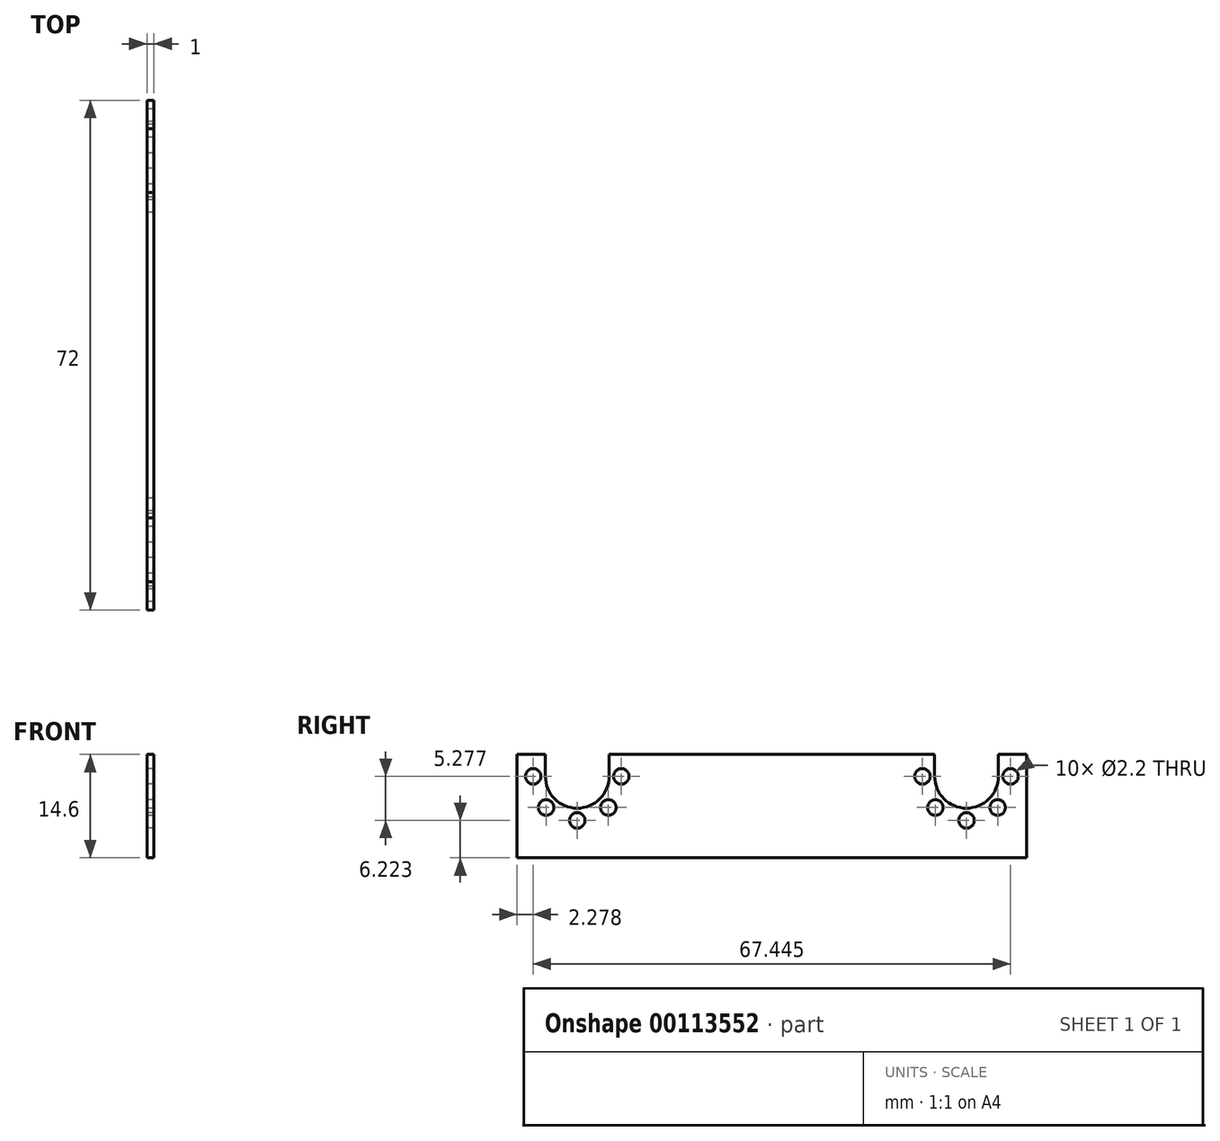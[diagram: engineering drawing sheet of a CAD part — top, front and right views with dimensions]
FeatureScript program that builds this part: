
annotation { "Feature Type Name" : "Feature", "Feature Type Description" : "" }
export const myFeature = defineFeature(function(context is Context, id is Id, definition is map)
    precondition{}
    {
        {
            var Q0;
            Q0=qCreatedBy(makeId("Front.planeOp"),FACE);
            var sketch = newSketch(context, id + "F0", { "sketchPlane" : qUnion([Q0])});
            skLineSegment(sketch, "E0", {"start": v(0, 20) * mm, "end": v(0, 0) * mm});
            skLineSegment(sketch, "E1", {"start": v(-1, 0) * mm, "end": v(-1, 20) * mm});
            skLineSegment(sketch, "E2", {"start": v(-1, 20) * mm, "end": v(0, 20) * mm});
            skLineSegment(sketch, "E3", {"start": v(-1, 0) * mm, "end": v(0, 0) * mm});
            skSolve(sketch);
        }
        {
            var Q0;
            Q0=qSketchRegion(id+"F0",true);
            extrude(context, id + "F1", {"entities" : qUnion([Q0]), "depth" : 72 * mm});
        }
        {
            var Q0;
            Q0=makeQuery(id+"F1.opExtrude","SWEPT_FACE",FACE,{"disambiguationData":[OSD([sQuery(id+"F0.wireOp",EDGE,"E1")])]});
            var sketch = newSketch(context, id + "F2", { "sketchPlane" : qUnion([Q0])});
            skArc(sketch, "E4", {"start": v(4, 11.5) * mm, "mid": v(8.5, 7) * mm, "end": v(13, 11.5) * mm});
            skCircle(sketch, "E5", {"center": v(2.28, 11.5) * mm, "radius": 1.1 * mm});
            skCircle(sketch, "E6.1.0", {"center": v(4.1, 7.1) * mm, "radius": 1.1 * mm});
            skCircle(sketch, "E6.2.0", {"center": v(8.5, 5.28) * mm, "radius": 1.1 * mm});
            skCircle(sketch, "E6.3.0", {"center": v(12.9, 7.1) * mm, "radius": 1.1 * mm});
            skCircle(sketch, "E7.1.4.0", {"center": v(14.72, 11.5) * mm, "radius": 1.1 * mm});
            skPoint(sketch, "E8", {"position": v(4, 11.5) * mm});
            skPoint(sketch, "E9", {"position": v(13, 11.5) * mm});
            skLineSegment(sketch, "E10", {"start": v(4, 11.5) * mm, "end": v(4, 20) * mm});
            skLineSegment(sketch, "E11", {"start": v(13, 11.5) * mm, "end": v(13, 20) * mm});
            skLineSegment(sketch, "E12", {"start": v(13, 20) * mm, "end": v(4, 20) * mm});
            skLineSegment(sketch, "E13", {"start": v(36, 20) * mm, "end": v(36, 0) * mm, "construction": true});
            skLineSegment(sketch, "E14.MirrorCS", {"start": v(68, 11.5) * mm, "end": v(68, 20) * mm});
            skCircle(sketch, "E15.MirrorC", {"center": v(69.72, 11.5) * mm, "radius": 1.1 * mm});
            skCircle(sketch, "E16.MirrorC", {"center": v(67.9, 7.1) * mm, "radius": 1.1 * mm});
            skCircle(sketch, "E17.MirrorC", {"center": v(63.5, 5.28) * mm, "radius": 1.1 * mm});
            skCircle(sketch, "E18.MirrorC", {"center": v(59.1, 7.1) * mm, "radius": 1.1 * mm});
            skCircle(sketch, "E19.MirrorC", {"center": v(57.28, 11.5) * mm, "radius": 1.1 * mm});
            skLineSegment(sketch, "E20.MirrorCS", {"start": v(59, 11.5) * mm, "end": v(59, 20) * mm});
            skLineSegment(sketch, "E21.MirrorCS", {"start": v(59, 20) * mm, "end": v(68, 20) * mm});
            skArc(sketch, "E22.MirrorCS", {"start": v(68, 11.5) * mm, "mid": v(63.5, 7) * mm, "end": v(59, 11.5) * mm});
            skSolve(sketch);
        }
        {
            var Q0;
            Q0=qSketchRegion(id+"F2",true);
            extrude(context, id + "F3", {"entities" : qUnion([Q0]), "operationType" : NewBodyOperationType.REMOVE, "endBound" : BoundingType.THROUGH_ALL, "oppositeDirection" : true, "depth" : 25 * mm});
        }
        {
            var Q0;
            Q0=makeQuery(id+"F1.opExtrude","SWEPT_FACE",FACE,{"disambiguationData":[OSD([sQuery(id+"F0.wireOp",EDGE,"E1")])]});
            var sketch = newSketch(context, id + "F4", { "sketchPlane" : qUnion([Q0])});
            skLineSegment(sketch, "E23.bottom", {"start": v(0, 20) * mm, "end": v(72, 20) * mm});
            skLineSegment(sketch, "E23.top", {"start": v(0, 14.6) * mm, "end": v(72, 14.6) * mm});
            skLineSegment(sketch, "E23.left", {"start": v(0, 20) * mm, "end": v(0, 14.6) * mm});
            skLineSegment(sketch, "E23.right", {"start": v(72, 20) * mm, "end": v(72, 14.6) * mm});
            skSolve(sketch);
        }
        {
            var Q0;
            Q0=qSketchRegion(id+"F4",true);
            extrude(context, id + "F5", {"entities" : qUnion([Q0]), "operationType" : NewBodyOperationType.REMOVE, "endBound" : BoundingType.THROUGH_ALL, "oppositeDirection" : true, "depth" : 25 * mm});
        }
    });
